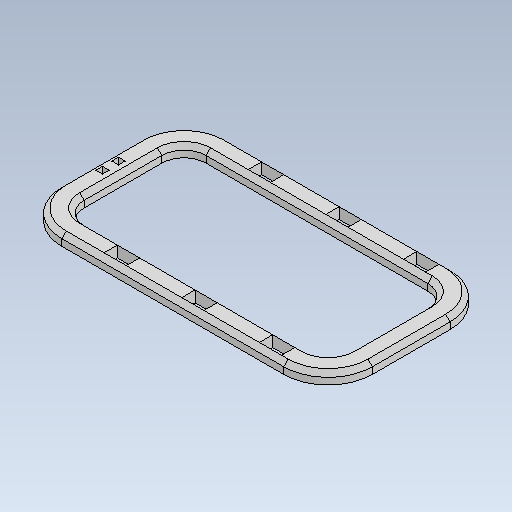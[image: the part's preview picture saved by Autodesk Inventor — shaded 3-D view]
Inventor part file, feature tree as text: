
AUTODESK INVENTOR PART (.ipt)
format: ipt  version: 2023 (Build 270158030, 158C)  size: 182,272 bytes
history: native  units: mm
features: reference x8, other x7, extrude x1, sketch x1
ambient origin geometry x8: Origin, YZ Plane, XZ Plane, XY Plane, X Axis, Y Axis, Z Axis, Center Point
bodies: Body1 (feature_tree)
feature tree (17):
  other  "V4.0-trebuchet-complete-parts.ipt"
  extrude  "Extrusion1"  TaperAngle=0.0deg  [1 undecoded]
  other  "baseplate::V4.0-trebuchet-complete-parts.ipt"
  other  "TaggingFeature1"
  sketch  "Sketch1"  dims[d0=10.0mm d1=0.0mm d2=0.0mm]
  reference  "Reference2"
  reference  "Reference3"
  reference  "Reference4"
  reference  "Reference5"
  reference  "Reference6"
  reference  "Reference7"
  reference  "Reference8"
  reference  "Reference9"
  other  "baseplate"
  other  "<userpath>\Documents\0004-inventor\3D-CAD-main\trebuchet\V4.0-trebuchet-assembled.iam"
  other  "V4.0-trebuchet-assembled.iam"
  other  "v4-latch:1"
note: 1 required parameter value undecoded (feature->parameter linkage not recoverable at this tier; creation-order binding heuristic only, values carry confidence <= 0.55)
